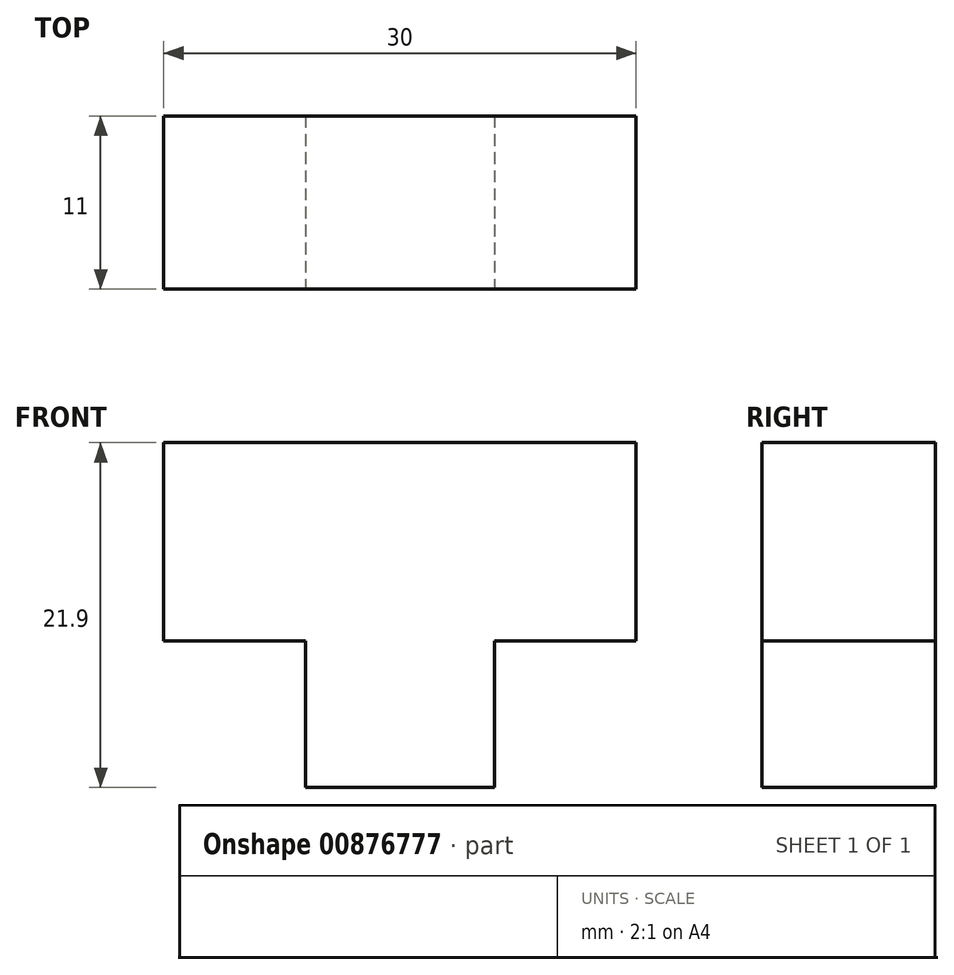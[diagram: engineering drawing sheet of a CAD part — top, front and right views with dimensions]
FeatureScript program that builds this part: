
annotation { "Feature Type Name" : "Feature", "Feature Type Description" : "" }
export const myFeature = defineFeature(function(context is Context, id is Id, definition is map)
    precondition{}
    {
        {
            var Q0;
            Q0=qCreatedBy(makeId("Front.planeOp"),FACE);
            var sketch = newSketch(context, id + "F0", { "sketchPlane" : qUnion([Q0])});
            skLineSegment(sketch, "E0.bottom", {"start": v(-15, -10.95) * mm, "end": v(15, -10.95) * mm});
            skLineSegment(sketch, "E0.top", {"start": v(-15, 10.95) * mm, "end": v(15, 10.95) * mm});
            skLineSegment(sketch, "E0.left", {"start": v(-15, -10.95) * mm, "end": v(-15, 10.95) * mm});
            skLineSegment(sketch, "E0.right", {"start": v(15, -10.95) * mm, "end": v(15, 10.95) * mm});
            skPoint(sketch, "E0.middle", {"position": v(0, 0) * mm});
            skSolve(sketch);
        }
        {
            var Q0;
            Q0 = qSketchRegion(id + "F0", true);
            extrude(context, id + "F1", {"entities" : qUnion([Q0]), "depth" : 11 * mm, "offsetDistance" : 25 * mm});
        }
        {
            var Q0;
            Q0=makeQuery(id+"F1.opExtrude","CAP_FACE",FACE,{"disambiguationData":[OSD([sQuery(id+"F0.wireOp",EDGE,"E0.bottom"),sQuery(id+"F0.wireOp",EDGE,"E0.top"),sQuery(id+"F0.wireOp",EDGE,"E0.left"),sQuery(id+"F0.wireOp",EDGE,"E0.right")])],"isStart":false});
            var sketch = newSketch(context, id + "F2", { "sketchPlane" : qUnion([Q0])});
            skLineSegment(sketch, "E1.bottom", {"start": v(-15, -10.95) * mm, "end": v(-6, -10.95) * mm});
            skLineSegment(sketch, "E1.top", {"start": v(-15, -1.65) * mm, "end": v(-6, -1.65) * mm});
            skLineSegment(sketch, "E1.left", {"start": v(-15, -10.95) * mm, "end": v(-15, -1.65) * mm});
            skLineSegment(sketch, "E1.right", {"start": v(-6, -10.95) * mm, "end": v(-6, -1.65) * mm});
            skLineSegment(sketch, "E2.MirrorCS", {"start": v(6, -10.95) * mm, "end": v(6, -1.65) * mm});
            skLineSegment(sketch, "E3.MirrorCS", {"start": v(15, -10.95) * mm, "end": v(15, -1.65) * mm});
            skLineSegment(sketch, "E4.MirrorCS", {"start": v(15, -10.95) * mm, "end": v(6, -10.95) * mm});
            skLineSegment(sketch, "E5.MirrorCS", {"start": v(15, -1.65) * mm, "end": v(6, -1.65) * mm});
            skSolve(sketch);
        }
        {
            var Q0;
            Q0 = qSketchRegion(id + "F2", true);
            extrude(context, id + "F3", {"entities" : qUnion([Q0]), "operationType" : NewBodyOperationType.REMOVE, "oppositeDirection" : true, "depth" : 25 * mm, "offsetDistance" : 25 * mm});
        }
    });
